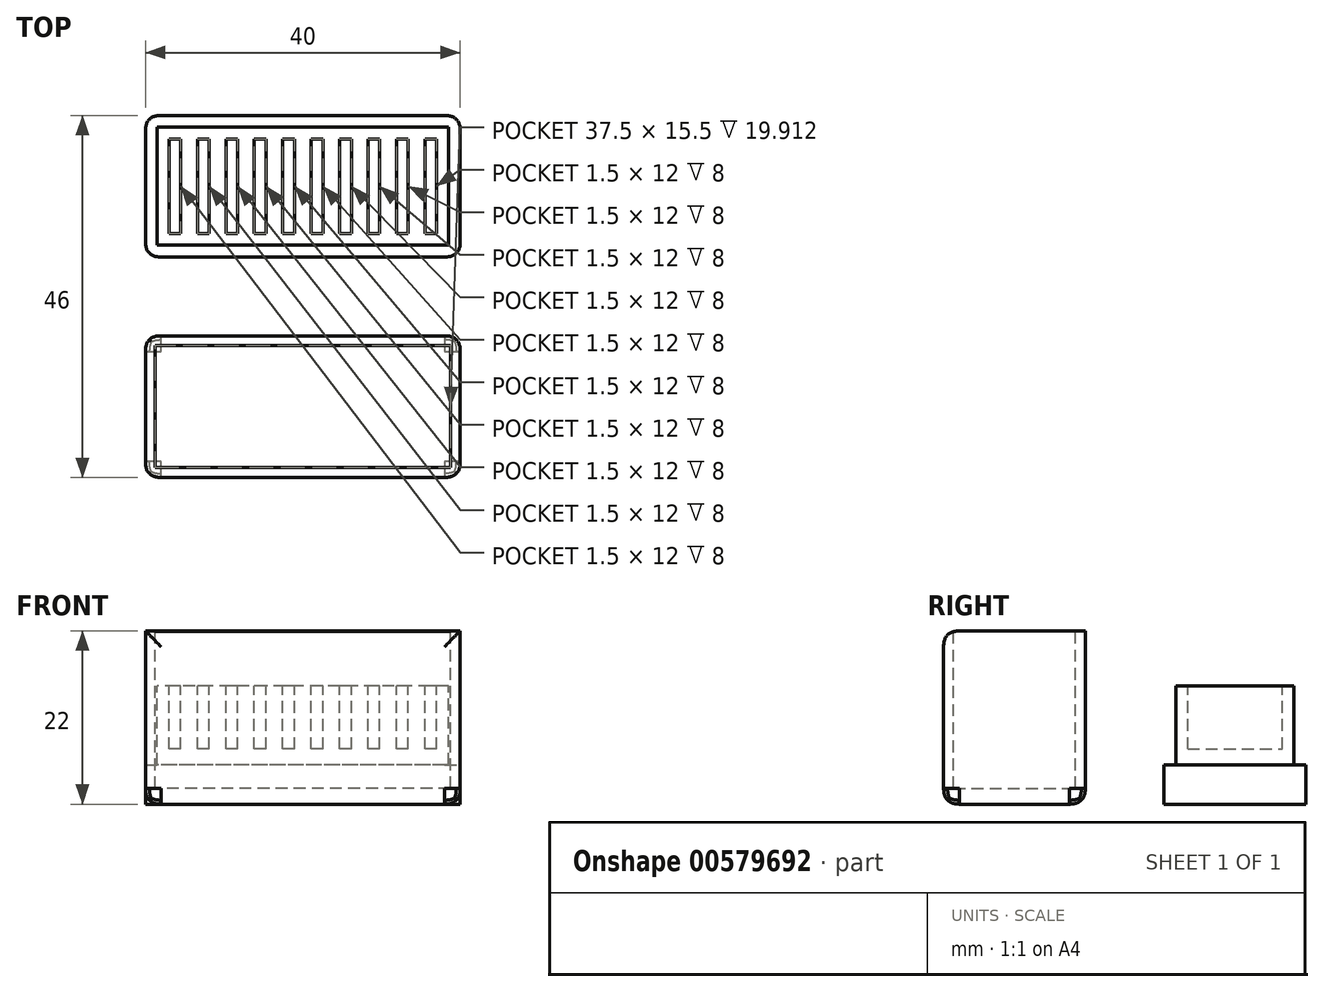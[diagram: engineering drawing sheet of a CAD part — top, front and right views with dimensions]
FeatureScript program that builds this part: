
annotation { "Feature Type Name" : "Feature", "Feature Type Description" : "" }
export const myFeature = defineFeature(function(context is Context, id is Id, definition is map)
    precondition{}
    {
        {
            var Q0;
            Q0=qCreatedBy(makeId("Top.planeOp"),FACE);
            var sketch = newSketch(context, id + "F0", { "sketchPlane" : qUnion([Q0])});
            skLineSegment(sketch, "E0.bottom", {"start": v(20, 9) * mm, "end": v(-20, 9) * mm});
            skLineSegment(sketch, "E0.top", {"start": v(20, -9) * mm, "end": v(-20, -9) * mm});
            skLineSegment(sketch, "E0.left", {"start": v(20, 9) * mm, "end": v(20, -9) * mm});
            skLineSegment(sketch, "E0.right", {"start": v(-20, 9) * mm, "end": v(-20, -9) * mm});
            skPoint(sketch, "E0.middle", {"position": v(0, 0) * mm});
            skSolve(sketch);
        }
        {
            var Q0;
            Q0 = qSketchRegion(id + "F0", true);
            extrude(context, id + "F1", {"entities" : qUnion([Q0]), "depth" : 15 * mm, "offsetDistance" : 25 * mm});
        }
        {
            var Q0;
            Q0=makeQuery(id+"F1.opExtrude","CAP_FACE",FACE,{"disambiguationData":[OSD([sQuery(id+"F0.wireOp",EDGE,"E0.bottom"),sQuery(id+"F0.wireOp",EDGE,"E0.top"),sQuery(id+"F0.wireOp",EDGE,"E0.left"),sQuery(id+"F0.wireOp",EDGE,"E0.right")])],"isStart":false});
            var sketch = newSketch(context, id + "F2", { "sketchPlane" : qUnion([Q0])});
            skLineSegment(sketch, "E1.bottom", {"start": v(-15.5, -6) * mm, "end": v(-17, -6) * mm});
            skLineSegment(sketch, "E1.top", {"start": v(-15.5, 6) * mm, "end": v(-17, 6) * mm});
            skLineSegment(sketch, "E1.left", {"start": v(-15.5, -6) * mm, "end": v(-15.5, 6) * mm});
            skLineSegment(sketch, "E1.right", {"start": v(-17, -6) * mm, "end": v(-17, 6) * mm});
            skPoint(sketch, "E1.middle", {"position": v(-16.25, 0) * mm});
            skLineSegment(sketch, "E2.1.0.0", {"start": v(-13.39, -6) * mm, "end": v(-13.39, 6) * mm});
            skLineSegment(sketch, "E2.1.0.1", {"start": v(-11.89, -6) * mm, "end": v(-13.39, -6) * mm});
            skPoint(sketch, "E2.1.0.2", {"position": v(-12.64, 0) * mm});
            skLineSegment(sketch, "E2.1.0.3", {"start": v(-11.89, -6) * mm, "end": v(-11.89, 6) * mm});
            skLineSegment(sketch, "E2.1.0.4", {"start": v(-11.89, 6) * mm, "end": v(-13.39, 6) * mm});
            skLineSegment(sketch, "E2.2.0.0", {"start": v(-9.78, -6) * mm, "end": v(-9.78, 6) * mm});
            skLineSegment(sketch, "E2.2.0.1", {"start": v(-8.28, -6) * mm, "end": v(-9.78, -6) * mm});
            skPoint(sketch, "E2.2.0.2", {"position": v(-9.03, 0) * mm});
            skLineSegment(sketch, "E2.2.0.3", {"start": v(-8.28, -6) * mm, "end": v(-8.28, 6) * mm});
            skLineSegment(sketch, "E2.2.0.4", {"start": v(-8.28, 6) * mm, "end": v(-9.78, 6) * mm});
            skLineSegment(sketch, "E2.3.0.0", {"start": v(-6.17, -6) * mm, "end": v(-6.17, 6) * mm});
            skLineSegment(sketch, "E2.3.0.1", {"start": v(-4.67, -6) * mm, "end": v(-6.17, -6) * mm});
            skPoint(sketch, "E2.3.0.2", {"position": v(-5.42, 0) * mm});
            skLineSegment(sketch, "E2.3.0.3", {"start": v(-4.67, -6) * mm, "end": v(-4.67, 6) * mm});
            skLineSegment(sketch, "E2.3.0.4", {"start": v(-4.67, 6) * mm, "end": v(-6.17, 6) * mm});
            skLineSegment(sketch, "E2.4.0.0", {"start": v(-2.56, -6) * mm, "end": v(-2.56, 6) * mm});
            skLineSegment(sketch, "E2.4.0.1", {"start": v(-1.06, -6) * mm, "end": v(-2.56, -6) * mm});
            skPoint(sketch, "E2.4.0.2", {"position": v(-1.8, 0) * mm});
            skLineSegment(sketch, "E2.4.0.3", {"start": v(-1.06, -6) * mm, "end": v(-1.06, 6) * mm});
            skLineSegment(sketch, "E2.4.0.4", {"start": v(-1.06, 6) * mm, "end": v(-2.56, 6) * mm});
            skLineSegment(sketch, "E2.5.0.0", {"start": v(1.06, -6) * mm, "end": v(1.06, 6) * mm});
            skLineSegment(sketch, "E2.5.0.1", {"start": v(2.56, -6) * mm, "end": v(1.06, -6) * mm});
            skPoint(sketch, "E2.5.0.2", {"position": v(1.8, 0) * mm});
            skLineSegment(sketch, "E2.5.0.3", {"start": v(2.56, -6) * mm, "end": v(2.56, 6) * mm});
            skLineSegment(sketch, "E2.5.0.4", {"start": v(2.56, 6) * mm, "end": v(1.06, 6) * mm});
            skLineSegment(sketch, "E2.6.0.0", {"start": v(4.67, -6) * mm, "end": v(4.67, 6) * mm});
            skLineSegment(sketch, "E2.6.0.1", {"start": v(6.17, -6) * mm, "end": v(4.67, -6) * mm});
            skPoint(sketch, "E2.6.0.2", {"position": v(5.42, 0) * mm});
            skLineSegment(sketch, "E2.6.0.3", {"start": v(6.17, -6) * mm, "end": v(6.17, 6) * mm});
            skLineSegment(sketch, "E2.6.0.4", {"start": v(6.17, 6) * mm, "end": v(4.67, 6) * mm});
            skLineSegment(sketch, "E2.7.0.0", {"start": v(8.28, -6) * mm, "end": v(8.28, 6) * mm});
            skLineSegment(sketch, "E2.7.0.1", {"start": v(9.78, -6) * mm, "end": v(8.28, -6) * mm});
            skPoint(sketch, "E2.7.0.2", {"position": v(9.03, 0) * mm});
            skLineSegment(sketch, "E2.7.0.3", {"start": v(9.78, -6) * mm, "end": v(9.78, 6) * mm});
            skLineSegment(sketch, "E2.7.0.4", {"start": v(9.78, 6) * mm, "end": v(8.28, 6) * mm});
            skLineSegment(sketch, "E2.8.0.0", {"start": v(11.89, -6) * mm, "end": v(11.89, 6) * mm});
            skLineSegment(sketch, "E2.8.0.1", {"start": v(13.39, -6) * mm, "end": v(11.89, -6) * mm});
            skPoint(sketch, "E2.8.0.2", {"position": v(12.64, 0) * mm});
            skLineSegment(sketch, "E2.8.0.3", {"start": v(13.39, -6) * mm, "end": v(13.39, 6) * mm});
            skLineSegment(sketch, "E2.8.0.4", {"start": v(13.39, 6) * mm, "end": v(11.89, 6) * mm});
            skLineSegment(sketch, "E2.9.0.0", {"start": v(15.5, -6) * mm, "end": v(15.5, 6) * mm});
            skLineSegment(sketch, "E2.9.0.1", {"start": v(17, -6) * mm, "end": v(15.5, -6) * mm});
            skPoint(sketch, "E2.9.0.2", {"position": v(16.25, 0) * mm});
            skLineSegment(sketch, "E2.9.0.3", {"start": v(17, -6) * mm, "end": v(17, 6) * mm});
            skLineSegment(sketch, "E2.9.0.4", {"start": v(17, 6) * mm, "end": v(15.5, 6) * mm});
            skLineSegment(sketch, "E2.direction1", {"start": v(-17, -6) * mm, "end": v(-13.39, -6) * mm, "construction": true});
            skSolve(sketch);
        }
        {
            var Q0;
            Q0 = qSketchRegion(id + "F2", true);
            extrude(context, id + "F3", {"entities" : qUnion([Q0]), "operationType" : NewBodyOperationType.REMOVE, "oppositeDirection" : true, "depth" : 8 * mm, "offsetDistance" : 25 * mm});
        }
        {
            var Q0;
            Q0=makeQuery(id+"F1.opExtrude","CAP_FACE",FACE,{"disambiguationData":[OSD([sQuery(id+"F0.wireOp",EDGE,"E0.bottom"),sQuery(id+"F0.wireOp",EDGE,"E0.top"),sQuery(id+"F0.wireOp",EDGE,"E0.left"),sQuery(id+"F0.wireOp",EDGE,"E0.right")])],"isStart":false});
            var sketch = newSketch(context, id + "F4", { "sketchPlane" : qUnion([Q0])});
            skLineSegment(sketch, "E3.bottom", {"start": v(18.5, 7.5) * mm, "end": v(-18.5, 7.5) * mm});
            skLineSegment(sketch, "E3.top", {"start": v(18.5, -7.5) * mm, "end": v(-18.5, -7.5) * mm});
            skLineSegment(sketch, "E3.left", {"start": v(18.5, 7.5) * mm, "end": v(18.5, -7.5) * mm});
            skLineSegment(sketch, "E3.right", {"start": v(-18.5, 7.5) * mm, "end": v(-18.5, -7.5) * mm});
            skPoint(sketch, "E3.middle", {"position": v(0, 0) * mm});
            skSolve(sketch);
        }
        {
            var Q0;
            Q0=makeQuery(id+"F4.imprint","IMPRINT",FACE,{"disambiguationData":[TD([[makeQuery(id+"F4.imprint","IMPRINT",EDGE,{"derivedFrom":sQuery(id+"F4.wireOp",EDGE,"E3.bottom")}),-1.0]])]});
            extrude(context, id + "F5", {"entities" : qUnion([Q0]), "operationType" : NewBodyOperationType.REMOVE, "oppositeDirection" : true, "depth" : 10 * mm, "offsetDistance" : 25 * mm});
        }
        {
            var Q0;
            Q0=qCreatedBy(makeId("Top.planeOp"),FACE);
            var sketch = newSketch(context, id + "F6", { "sketchPlane" : qUnion([Q0])});
            skLineSegment(sketch, "E4.bottom", {"start": v(20, -37) * mm, "end": v(-20, -37) * mm});
            skLineSegment(sketch, "E4.top", {"start": v(20, -19) * mm, "end": v(-20, -19) * mm});
            skLineSegment(sketch, "E4.left", {"start": v(20, -37) * mm, "end": v(20, -19) * mm});
            skLineSegment(sketch, "E4.right", {"start": v(-20, -37) * mm, "end": v(-20, -19) * mm});
            skPoint(sketch, "E4.middle", {"position": v(0, -28) * mm});
            skSolve(sketch);
        }
        {
            var Q0;
            Q0 = qSketchRegion(id + "F6", true);
            extrude(context, id + "F7", {"entities" : qUnion([Q0]), "depth" : 22 * mm, "offsetDistance" : 25 * mm});
        }
        {
            var Q0;
            Q0=makeQuery(id+"F7.opExtrude","CAP_FACE",FACE,{"disambiguationData":[OSD([sQuery(id+"F6.wireOp",EDGE,"E4.bottom"),sQuery(id+"F6.wireOp",EDGE,"E4.top"),sQuery(id+"F6.wireOp",EDGE,"E4.left"),sQuery(id+"F6.wireOp",EDGE,"E4.right")])],"isStart":false});
            var sketch = newSketch(context, id + "F8", { "sketchPlane" : qUnion([Q0])});
            skLineSegment(sketch, "E5.bottom", {"start": v(18.75, -35.75) * mm, "end": v(-18.75, -35.75) * mm});
            skLineSegment(sketch, "E5.top", {"start": v(18.75, -20.25) * mm, "end": v(-18.75, -20.25) * mm});
            skLineSegment(sketch, "E5.left", {"start": v(18.75, -35.75) * mm, "end": v(18.75, -20.25) * mm});
            skLineSegment(sketch, "E5.right", {"start": v(-18.75, -35.75) * mm, "end": v(-18.75, -20.25) * mm});
            skPoint(sketch, "E5.middle", {"position": v(0, -28) * mm});
            skPoint(sketch, "E5.middle.positionSnap0", {"position": v(0, -19) * mm});
            skPoint(sketch, "E5.middle.positionSnap1", {"position": v(-20, -28) * mm});
            skPoint(sketch, "E5.centerSnap0", {"position": v(0, -19) * mm});
            skPoint(sketch, "E5.centerSnap1", {"position": v(-20, -28) * mm});
            skSolve(sketch);
        }
        {
            var Q0;
            Q0 = qSketchRegion(id + "F8", true);
            extrude(context, id + "F9", {"entities" : qUnion([Q0]), "operationType" : NewBodyOperationType.REMOVE, "oppositeDirection" : true, "depth" : 20 * mm, "offsetDistance" : 25 * mm});
        }
        {
            var Q0;
            Q0=makeQuery(id+"F7.opExtrude","CAP_EDGE",EDGE,{"disambiguationData":[OSD([sQuery(id+"F6.wireOp",EDGE,"E4.bottom")])],"isStart":true});
            var Q1;
            Q1=makeQuery(id+"F7.opExtrude","CAP_EDGE",EDGE,{"disambiguationData":[OSD([sQuery(id+"F6.wireOp",EDGE,"E4.top")])],"isStart":true});
            var Q2;
            Q2=makeQuery(id+"F7.opExtrude","CAP_EDGE",EDGE,{"disambiguationData":[OSD([sQuery(id+"F6.wireOp",EDGE,"E4.left")])],"isStart":true});
            var Q3;
            Q3=makeQuery(id+"F7.opExtrude","CAP_EDGE",EDGE,{"disambiguationData":[OSD([sQuery(id+"F6.wireOp",EDGE,"E4.right")])],"isStart":true});
            var Q4;
            Q4=makeQuery(id+"F7.opExtrude","SWEPT_EDGE",EDGE,{"disambiguationData":[OSD([sQuery(id+"F6.wireOp",EDGE,"E4.bottom"),sQuery(id+"F6.wireOp",EDGE,"E4.left")])]});
            var Q5;
            Q5=makeQuery(id+"F7.opExtrude","SWEPT_EDGE",EDGE,{"disambiguationData":[OSD([sQuery(id+"F6.wireOp",EDGE,"E4.top"),sQuery(id+"F6.wireOp",EDGE,"E4.left")])]});
            var Q6;
            Q6=makeQuery(id+"F7.opExtrude","SWEPT_EDGE",EDGE,{"disambiguationData":[OSD([sQuery(id+"F6.wireOp",EDGE,"E4.top"),sQuery(id+"F6.wireOp",EDGE,"E4.right")])]});
            var Q7;
            Q7=makeQuery(id+"F7.opExtrude","SWEPT_FACE",FACE,{"disambiguationData":[OSD([sQuery(id+"F6.wireOp",EDGE,"E4.bottom")])]});
            var Q8;
            Q8=makeQuery(id+"F1.opExtrude","SWEPT_EDGE",EDGE,{"disambiguationData":[OSD([sQuery(id+"F0.wireOp",EDGE,"E0.bottom"),sQuery(id+"F0.wireOp",EDGE,"E0.left")])]});
            var Q9;
            Q9=makeQuery(id+"F1.opExtrude","SWEPT_EDGE",EDGE,{"disambiguationData":[OSD([sQuery(id+"F0.wireOp",EDGE,"E0.top"),sQuery(id+"F0.wireOp",EDGE,"E0.left")])]});
            var Q10;
            Q10=makeQuery(id+"F1.opExtrude","SWEPT_EDGE",EDGE,{"disambiguationData":[OSD([sQuery(id+"F0.wireOp",EDGE,"E0.top"),sQuery(id+"F0.wireOp",EDGE,"E0.right")])]});
            var Q11;
            Q11=makeQuery(id+"F1.opExtrude","SWEPT_EDGE",EDGE,{"disambiguationData":[OSD([sQuery(id+"F0.wireOp",EDGE,"E0.bottom"),sQuery(id+"F0.wireOp",EDGE,"E0.right")])]});
            fillet(context, id + "F10", {"entities" : qUnion([Q0, Q1, Q2, Q3, Q4, Q5, Q6, Q7, Q8, Q9, Q10, Q11]), "radius" : 2 * mm, "tangentPropagation" : true, "rho" : 0.5, "crossSection" : FilletCrossSection.CONIC, "allowEdgeOverflow" : false});
        }
    });
